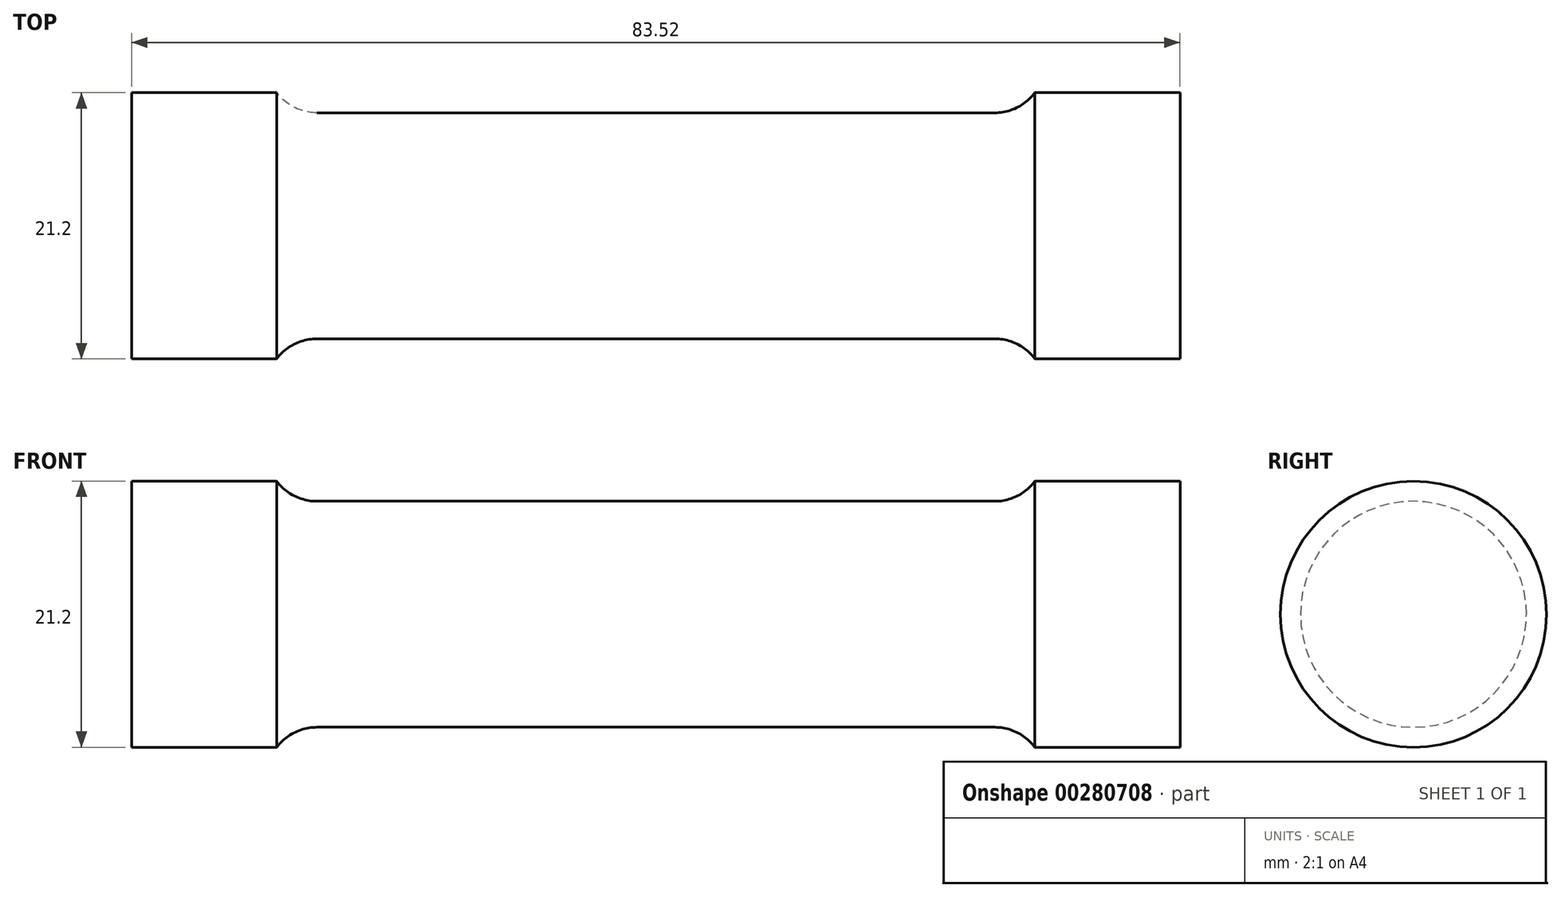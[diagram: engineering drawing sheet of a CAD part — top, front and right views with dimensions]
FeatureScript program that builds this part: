
annotation { "Feature Type Name" : "Feature", "Feature Type Description" : "" }
export const myFeature = defineFeature(function(context is Context, id is Id, definition is map)
    precondition{}
    {
        {
            var Q0;
            Q0=qCreatedBy(makeId("Front.planeOp"),FACE);
            var sketch = newSketch(context, id + "F0", { "sketchPlane" : qUnion([Q0])});
            skLineSegment(sketch, "E0", {"start": v(0, 9) * mm, "end": v(27, 9) * mm});
            skArc(sketch, "E1", {"start": v(27, 9) * mm, "mid": v(28.79, 9.42) * mm, "end": v(30.2, 10.6) * mm});
            skLineSegment(sketch, "E2", {"start": v(30.2, 10.6) * mm, "end": v(41.76, 10.6) * mm});
            skLineSegment(sketch, "E3", {"start": v(41.76, 10.6) * mm, "end": v(41.76, 0) * mm});
            skLineSegment(sketch, "E4.MirrorCS", {"start": v(0, 9) * mm, "end": v(-27, 9) * mm});
            skLineSegment(sketch, "E5.MirrorCS", {"start": v(-41.76, 10.6) * mm, "end": v(-41.76, 0) * mm});
            skLineSegment(sketch, "E6.MirrorCS", {"start": v(-30.2, 10.6) * mm, "end": v(-41.76, 10.6) * mm});
            skArc(sketch, "E7.MirrorCS", {"start": v(-27, 9) * mm, "mid": v(-28.79, 9.42) * mm, "end": v(-30.2, 10.6) * mm});
            skLineSegment(sketch, "E8", {"start": v(-41.76, 0) * mm, "end": v(41.76, 0) * mm});
            skSolve(sketch);
        }
        {
            var Q0;
            Q0 = qSketchRegion(id + "F0", true);
            var Q1;
            Q1=sQuery(id+"F0.wireOp",EDGE,"E8");
            revolve(context, id + "F1", {"entities" : qUnion([Q0]), "axis" : qUnion([Q1]), "revolveType" : RevolveType.FULL});
        }
    });
